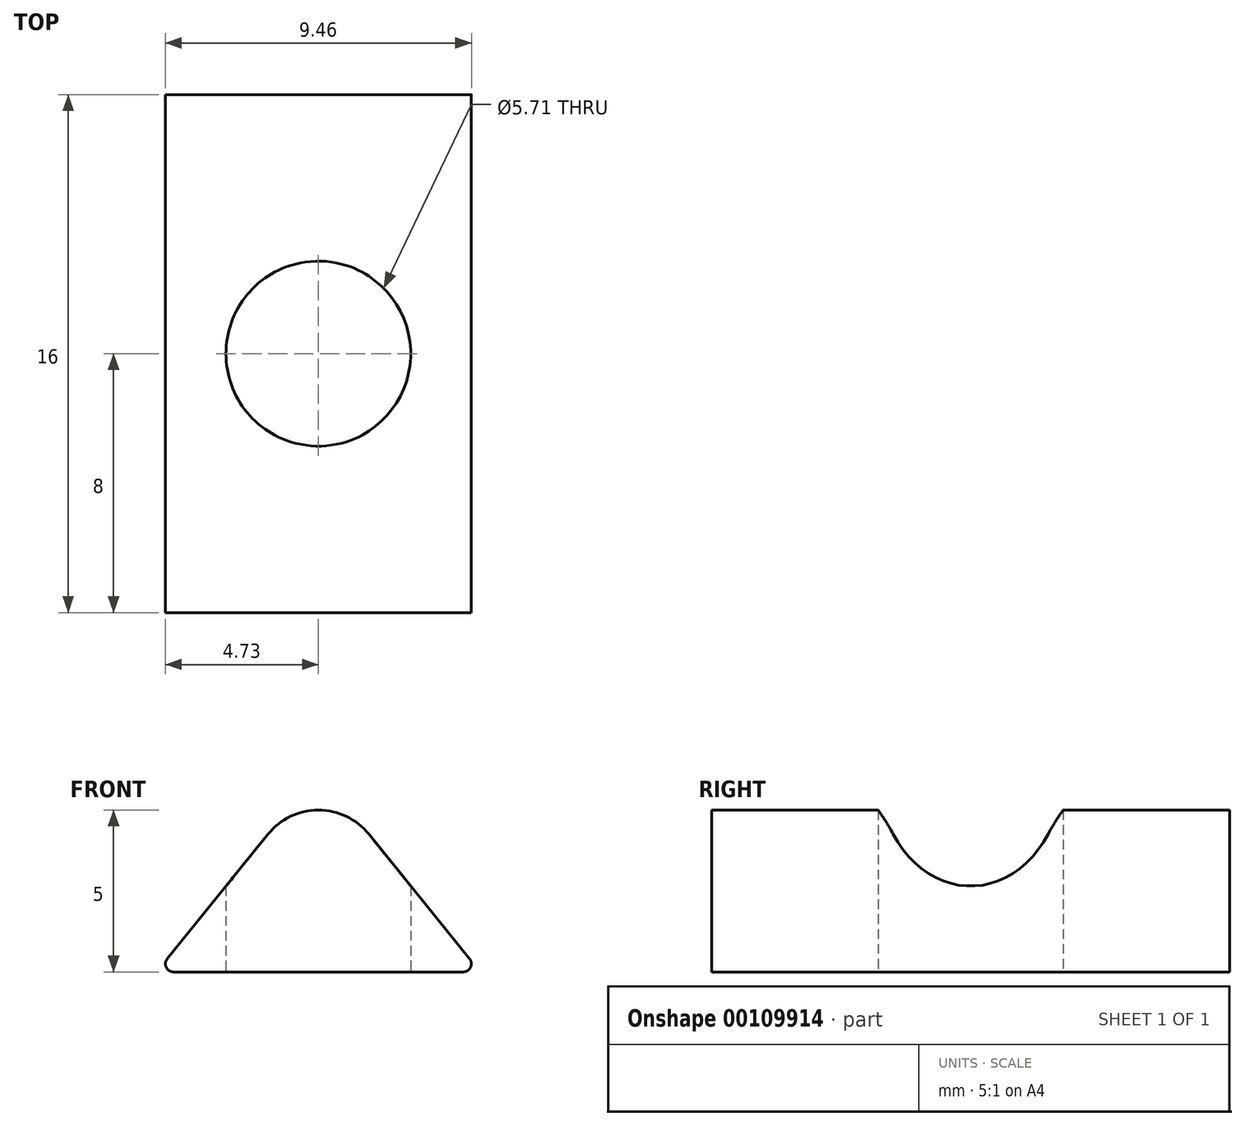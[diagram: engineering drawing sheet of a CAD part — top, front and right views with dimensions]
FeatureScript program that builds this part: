
annotation { "Feature Type Name" : "Feature", "Feature Type Description" : "" }
export const myFeature = defineFeature(function(context is Context, id is Id, definition is map)
    precondition{}
    {
        {
            var Q0;
            Q0=qCreatedBy(makeId("Front.planeOp"),FACE);
            var sketch = newSketch(context, id + "F0", { "sketchPlane" : qUnion([Q0])});
            skLineSegment(sketch, "E0", {"start": v(-4.48, 0) * mm, "end": v(4.48, 0) * mm});
            skLineSegment(sketch, "E1", {"start": v(4.67, 0.4) * mm, "end": v(1.55, 4.26) * mm});
            skLineSegment(sketch, "E2", {"start": v(-4.67, 0.4) * mm, "end": v(-1.55, 4.26) * mm});
            skArc(sketch, "E3", {"start": v(1.55, 4.26) * mm, "mid": v(0, 5) * mm, "end": v(-1.55, 4.26) * mm});
            skPoint(sketch, "E4.visualSharp", {"position": v(-5, 0) * mm});
            skArc(sketch, "E4.filletArc", {"start": v(-4.67, 0.4) * mm, "mid": v(-4.7, 0.14) * mm, "end": v(-4.48, 0) * mm});
            skPoint(sketch, "E5.visualSharp", {"position": v(5, 0) * mm});
            skArc(sketch, "E5.filletArc", {"start": v(4.48, 0) * mm, "mid": v(4.7, 0.14) * mm, "end": v(4.67, 0.4) * mm});
            skSolve(sketch);
        }
        {
            var Q0;
            Q0=makeQuery(id+"F0.imprint","IMPRINT",FACE,{"disambiguationData":[TD([[makeQuery(id+"F0.imprint","IMPRINT",EDGE,{"derivedFrom":sQuery(id+"F0.wireOp",EDGE,"E0")}),1.0]])]});
            extrude(context, id + "F1", {"entities" : qUnion([Q0]), "depth" : 16 * mm});
        }
        {
            var Q0;
            Q0=makeQuery(id+"F1.opExtrude","SWEPT_FACE",FACE,{"disambiguationData":[OSD([sQuery(id+"F0.wireOp",EDGE,"E0")])]});
            var sketch = newSketch(context, id + "F2", { "sketchPlane" : qUnion([Q0])});
            skCircle(sketch, "E6", {"center": v(0, 8) * mm, "radius": 2.86 * mm});
            skSolve(sketch);
        }
        {
            var Q0;
            Q0=makeQuery(id+"F2.imprint","IMPRINT",FACE,{"disambiguationData":[TD([[makeQuery(id+"F2.imprint","IMPRINT",EDGE,{"derivedFrom":sQuery(id+"F2.wireOp",EDGE,"E6")}),1.0]])]});
            extrude(context, id + "F3", {"entities" : qUnion([Q0]), "operationType" : NewBodyOperationType.REMOVE, "endBound" : BoundingType.THROUGH_ALL, "oppositeDirection" : true, "depth" : 25 * mm});
        }
    });
